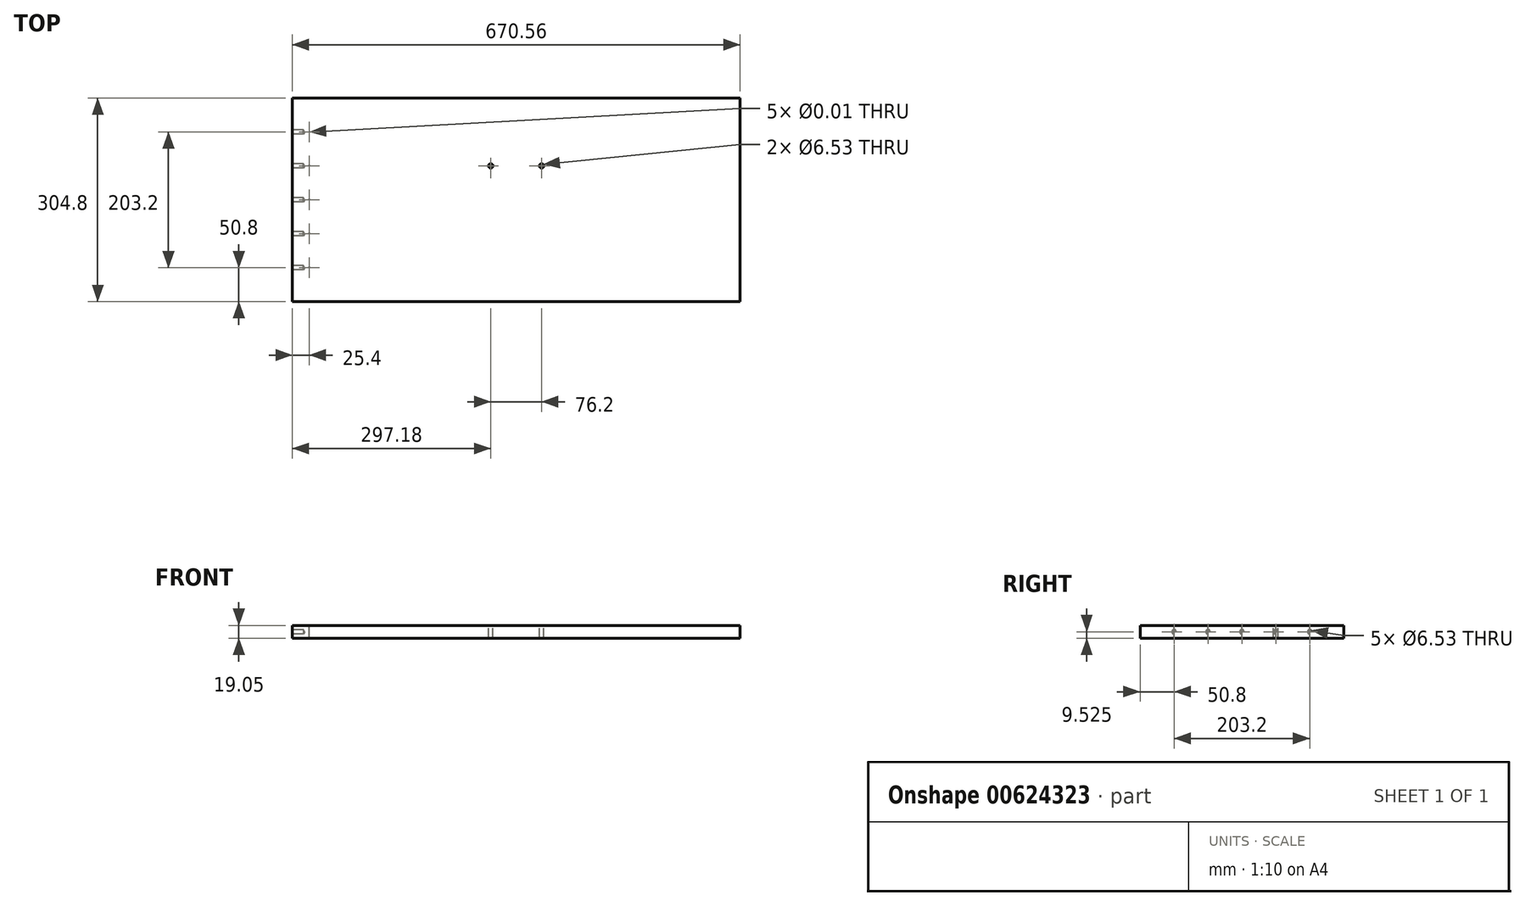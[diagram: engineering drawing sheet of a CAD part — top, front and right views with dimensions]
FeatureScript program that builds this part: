
annotation { "Feature Type Name" : "Feature", "Feature Type Description" : "" }
export const myFeature = defineFeature(function(context is Context, id is Id, definition is map)
    precondition{}
    {
        {
            var Q0;
            Q0=qCreatedBy(makeId("Top.planeOp"),FACE);
            var sketch = newSketch(context, id + "F0", { "sketchPlane" : qUnion([Q0])});
            skLineSegment(sketch, "E0.bottom", {"start": v(-335.28, 152.4) * mm, "end": v(335.28, 152.4) * mm});
            skLineSegment(sketch, "E0.top", {"start": v(-335.28, -152.4) * mm, "end": v(335.28, -152.4) * mm});
            skLineSegment(sketch, "E0.left", {"start": v(-335.28, 152.4) * mm, "end": v(-335.28, -152.4) * mm});
            skLineSegment(sketch, "E0.right", {"start": v(335.28, 152.4) * mm, "end": v(335.28, -152.4) * mm});
            skLineSegment(sketch, "E1", {"start": v(-335.28, 0) * mm, "end": v(335.28, 0) * mm, "construction": true});
            skLineSegment(sketch, "E2", {"start": v(0, 152.4) * mm, "end": v(0, -152.4) * mm, "construction": true});
            skPoint(sketch, "E3", {"position": v(-309.88, 101.6) * mm});
            skPoint(sketch, "E4.0.1.0", {"position": v(-309.88, 50.8) * mm});
            skPoint(sketch, "E4.0.2.0", {"position": v(-309.88, 0) * mm});
            skPoint(sketch, "E4.0.3.0", {"position": v(-309.88, -50.8) * mm});
            skPoint(sketch, "E4.0.4.0", {"position": v(-309.88, -101.6) * mm});
            skLineSegment(sketch, "E4.direction1", {"start": v(-309.88, 101.6) * mm, "end": v(-300.35, 101.6) * mm, "construction": true});
            skLineSegment(sketch, "E4.direction2", {"start": v(-309.88, 101.6) * mm, "end": v(-309.88, 50.8) * mm, "construction": true});
            skSolve(sketch);
        }
        {
            var Q0;
            Q0=makeQuery(id+"F0.imprint","IMPRINT",FACE,{"disambiguationData":[TD([[makeQuery(id+"F0.imprint","IMPRINT",EDGE,{"derivedFrom":sQuery(id+"F0.wireOp",EDGE,"E0.bottom")}),-1.0]])]});
            extrude(context, id + "F1", {"entities" : qUnion([Q0]), "oppositeDirection" : true, "depth" : 19.05 * mm, "offsetDistance" : 25.4 * mm});
        }
        {
            var Q0;
            Q0=sQuery(id+"F0.wireOp",VERTEX,"E3");
            var Q1;
            Q1=sQuery(id+"F0.wireOp",VERTEX,"E4.0.1.0");
            var Q2;
            Q2=sQuery(id+"F0.wireOp",VERTEX,"E4.0.2.0");
            var Q3;
            Q3=sQuery(id+"F0.wireOp",VERTEX,"E4.0.3.0");
            var Q4;
            Q4=sQuery(id+"F0.wireOp",VERTEX,"E4.0.4.0");
            var Q5;
            Q5=makeQuery(id+"F1.opExtrude","SWEPT_BODY",BODY,{"disambiguationData":[OSD([sQuery(id+"F0.wireOp",EDGE,"E0.bottom"),sQuery(id+"F0.wireOp",EDGE,"E0.top"),sQuery(id+"F0.wireOp",EDGE,"E0.left"),sQuery(id+"F0.wireOp",EDGE,"E0.right")])]});
            hole(context, id + "F2", {"style" : HoleStyle.SIMPLE, "endStyle" : HoleEndStyle.BLIND, "standardTappedOrClearance" : lookupTablePath({ "standard" : "ANSI", "size" : "3/8 (0.38)", "type" : "Drilled" }), "standardBlindInLast" : lookupTablePath({ "standard" : "ANSI", "size" : "3/8", "type" : "Drilled" }), "holeDiameter" : 3 / 203.2 * mm, "majorDiameter" : 6.35 * mm, "holeDepth" : 16.54 * mm, "isTappedThrough" : true, "tappedDepth" : 12.7 * mm, "tapClearance" : 3, "startFromSketch" : true, "locations" : qUnion([Q0, Q1, Q2, Q3, Q4]), "scope" : qUnion([Q5])});
        }
        {
            var Q0;
            Q0=makeQuery(id+"F1.opExtrude","SWEPT_FACE",FACE,{"disambiguationData":[OSD([sQuery(id+"F0.wireOp",EDGE,"E0.left")])]});
            var sketch = newSketch(context, id + "F3", { "sketchPlane" : qUnion([Q0])});
            skLineSegment(sketch, "E5", {"start": v(-152.4, -9.53) * mm, "end": v(152.4, -9.53) * mm, "construction": true});
            skPoint(sketch, "E6.0", {"position": v(-101.6, 0) * mm});
            skLineSegment(sketch, "E7", {"start": v(-101.6, 0) * mm, "end": v(-101.6, -9.53) * mm, "construction": true});
            skPoint(sketch, "E8", {"position": v(-101.6, -9.53) * mm});
            skPoint(sketch, "E9.1.0.0", {"position": v(-50.8, -9.53) * mm});
            skPoint(sketch, "E9.2.0.0", {"position": v(0, -9.53) * mm});
            skPoint(sketch, "E9.3.0.0", {"position": v(50.8, -9.53) * mm});
            skPoint(sketch, "E9.4.0.0", {"position": v(101.6, -9.53) * mm});
            skLineSegment(sketch, "E9.direction1", {"start": v(-101.6, -9.53) * mm, "end": v(-50.8, -9.53) * mm, "construction": true});
            skSolve(sketch);
        }
        {
            var Q0;
            Q0=sQuery(id+"F3.wireOp",VERTEX,"E8");
            var Q1;
            Q1=sQuery(id+"F3.wireOp",VERTEX,"E9.1.0.0");
            var Q2;
            Q2=sQuery(id+"F3.wireOp",VERTEX,"E9.2.0.0");
            var Q3;
            Q3=sQuery(id+"F3.wireOp",VERTEX,"E9.3.0.0");
            var Q4;
            Q4=sQuery(id+"F3.wireOp",VERTEX,"E9.4.0.0");
            var Q5;
            Q5=makeQuery(id+"F1.opExtrude","SWEPT_BODY",BODY,{"disambiguationData":[OSD([sQuery(id+"F0.wireOp",EDGE,"E0.bottom"),sQuery(id+"F0.wireOp",EDGE,"E0.top"),sQuery(id+"F0.wireOp",EDGE,"E0.left"),sQuery(id+"F0.wireOp",EDGE,"E0.right")])]});
            hole(context, id + "F4", {"style" : HoleStyle.SIMPLE, "endStyle" : HoleEndStyle.BLIND, "standardTappedOrClearance" : lookupTablePath({ "standard" : "ANSI", "fit" : "Close", "size" : "1/4", "type" : "Clearance" }), "standardBlindInLast" : lookupTablePath({ "fit" : "Close", "standard" : "ANSI", "size" : "1/4", "type" : "Clearance" }), "holeDiameter" : 6.53 * mm, "majorDiameter" : 6.35 * mm, "holeDepth" : 16.54 * mm, "isTappedThrough" : true, "tappedDepth" : 12.7 * mm, "tapClearance" : 3, "startFromSketch" : true, "locations" : qUnion([Q0, Q1, Q2, Q3, Q4]), "scope" : qUnion([Q5])});
        }
        {
            var Q0;
            Q0=makeQuery(id+"F0.imprint","IMPRINT",FACE,{"disambiguationData":[TD([[makeQuery(id+"F0.imprint","IMPRINT",EDGE,{"derivedFrom":sQuery(id+"F0.wireOp",EDGE,"E0.bottom")}),-1.0]])]});
            var sketch = newSketch(context, id + "F5", { "sketchPlane" : qUnion([Q0])});
            skPoint(sketch, "E10", {"position": v(-38.1, 50.8) * mm});
            skPoint(sketch, "E11.1.0.0", {"position": v(38.1, 50.8) * mm});
            skLineSegment(sketch, "E11.direction1", {"start": v(-38.1, 50.8) * mm, "end": v(38.1, 50.8) * mm, "construction": true});
            skSolve(sketch);
        }
        {
            var Q0;
            Q0=sQuery(id+"F5.wireOp",VERTEX,"E10");
            var Q1;
            Q1=sQuery(id+"F5.wireOp",VERTEX,"E11.1.0.0");
            var Q2;
            Q2=makeQuery(id+"F1.opExtrude","SWEPT_BODY",BODY,{"disambiguationData":[OSD([sQuery(id+"F0.wireOp",EDGE,"E0.bottom"),sQuery(id+"F0.wireOp",EDGE,"E0.top"),sQuery(id+"F0.wireOp",EDGE,"E0.left"),sQuery(id+"F0.wireOp",EDGE,"E0.right")])]});
            hole(context, id + "F6", {"style" : HoleStyle.SIMPLE, "endStyle" : HoleEndStyle.THROUGH, "standardTappedOrClearance" : lookupTablePath({ "standard" : "ANSI", "fit" : "Close", "size" : "1/4", "type" : "Clearance" }), "standardBlindInLast" : lookupTablePath({ "fit" : "Close", "standard" : "ANSI", "size" : "1/4", "type" : "Clearance" }), "holeDiameter" : 6.53 * mm, "majorDiameter" : 6.35 * mm, "isTappedThrough" : true, "tappedDepth" : 12.7 * mm, "tapClearance" : 3, "startFromSketch" : true, "locations" : qUnion([Q0, Q1]), "scope" : qUnion([Q2])});
        }
    });
